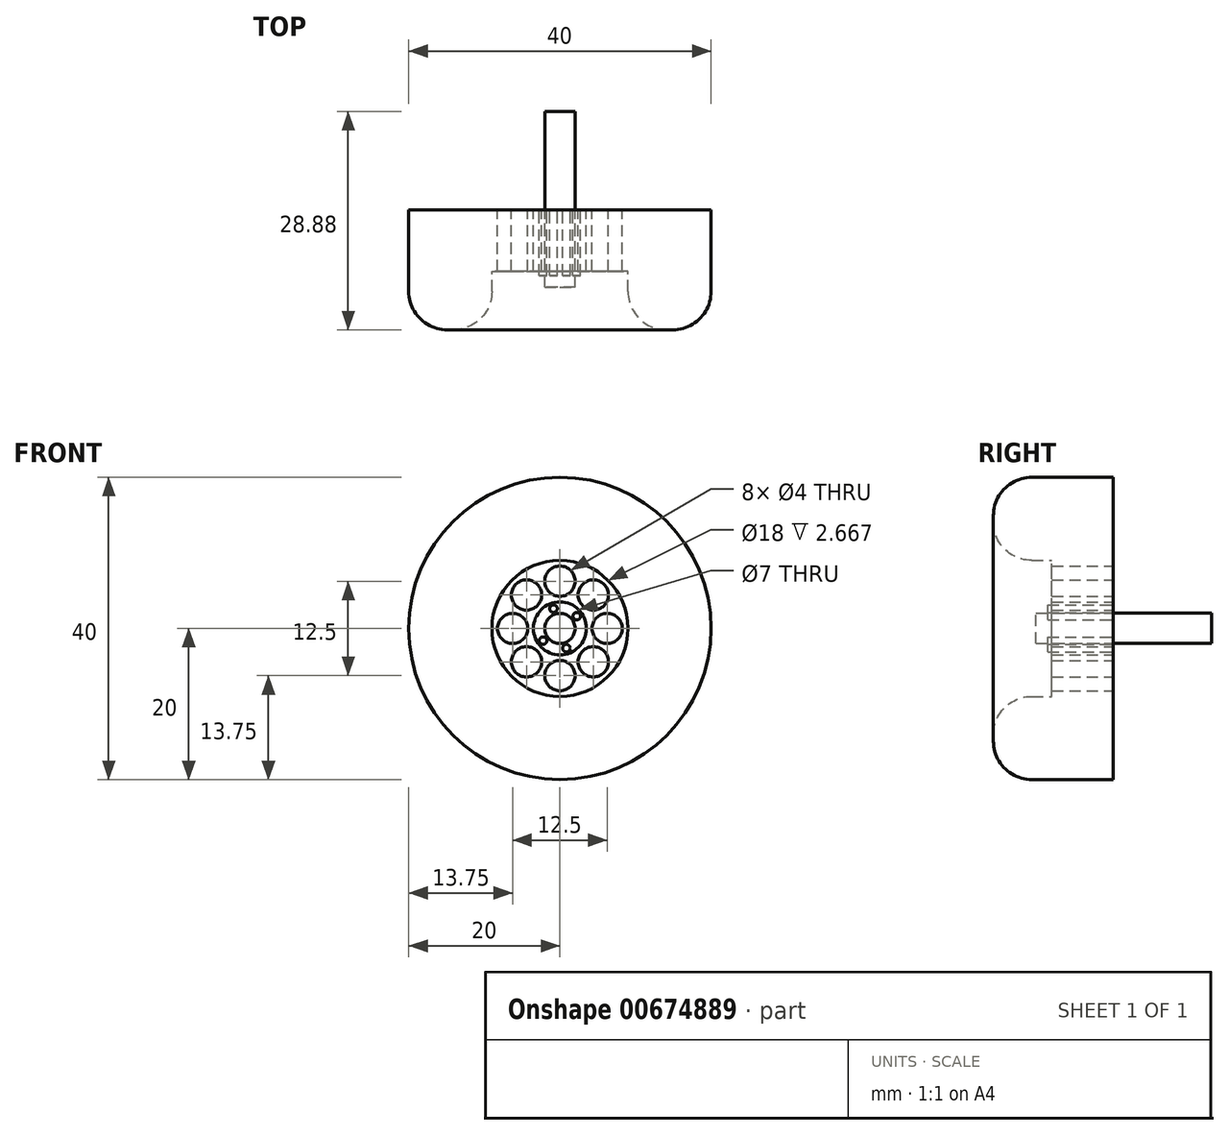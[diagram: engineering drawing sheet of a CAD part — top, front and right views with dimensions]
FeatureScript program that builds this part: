
annotation { "Feature Type Name" : "Feature", "Feature Type Description" : "" }
export const myFeature = defineFeature(function(context is Context, id is Id, definition is map)
    precondition{}
    {
        {
            var Q0;
            Q0=qCreatedBy(makeId("Front.planeOp"),FACE);
            var sketch = newSketch(context, id + "F0", { "sketchPlane" : qUnion([Q0])});
            skCircle(sketch, "E0", {"center": v(0, 0) * mm, "radius": 20 * mm});
            skSolve(sketch);
        }
        {
            var Q0;
            Q0=makeQuery(id+"F0.imprint","IMPRINT",FACE,{"disambiguationData":[TD([[makeQuery(id+"F0.imprint","IMPRINT",EDGE,{"derivedFrom":sQuery(id+"F0.wireOp",EDGE,"E0")}),1.0]])]});
            var sketch = newSketch(context, id + "F1", { "sketchPlane" : qUnion([Q0])});
            skCircle(sketch, "E1", {"center": v(0, 0) * mm, "radius": 3.5 * mm});
            skCircle(sketch, "E2", {"center": v(0, 0) * mm, "radius": 18 * mm});
            skCircle(sketch, "E3", {"center": v(0, 0) * mm, "radius": 2 * mm});
            skLineSegment(sketch, "E4", {"start": v(0, 18) * mm, "end": v(0, -18) * mm});
            skLineSegment(sketch, "E5", {"start": v(-18, 0) * mm, "end": v(18, 0) * mm});
            skCircle(sketch, "E6", {"center": v(0, 0) * mm, "radius": 9 * mm});
            skCircle(sketch, "E7", {"center": v(-2.75, 0) * mm, "radius": 0.5 * mm});
            skCircle(sketch, "E8", {"center": v(0, 6.25) * mm, "radius": 2 * mm});
            skCircle(sketch, "E9.1.0", {"center": v(-4.42, 4.42) * mm, "radius": 2 * mm});
            skCircle(sketch, "E9.2.0", {"center": v(-6.25, 0) * mm, "radius": 2 * mm});
            skCircle(sketch, "E9.3.0", {"center": v(-4.42, -4.42) * mm, "radius": 2 * mm});
            skCircle(sketch, "E9.4.0", {"center": v(0, -6.25) * mm, "radius": 2 * mm});
            skCircle(sketch, "E9.5.0", {"center": v(4.42, -4.42) * mm, "radius": 2 * mm});
            skCircle(sketch, "E9.6.0", {"center": v(6.25, 0) * mm, "radius": 2 * mm});
            skCircle(sketch, "E9.7.0", {"center": v(4.42, 4.42) * mm, "radius": 2 * mm});
            skCircle(sketch, "E10.1.0", {"center": v(-2.22, -1.62) * mm, "radius": 0.5 * mm});
            skCircle(sketch, "E10.2.0", {"center": v(-0.85, -2.62) * mm, "radius": 0.5 * mm});
            skCircle(sketch, "E10.3.0", {"center": v(0.85, -2.62) * mm, "radius": 0.5 * mm});
            skCircle(sketch, "E10.4.0", {"center": v(2.22, -1.62) * mm, "radius": 0.5 * mm});
            skCircle(sketch, "E10.5.0", {"center": v(2.75, 0) * mm, "radius": 0.5 * mm});
            skCircle(sketch, "E10.6.0", {"center": v(2.22, 1.62) * mm, "radius": 0.5 * mm});
            skCircle(sketch, "E10.7.0", {"center": v(0.85, 2.62) * mm, "radius": 0.5 * mm});
            skCircle(sketch, "E10.8.0", {"center": v(-0.85, 2.62) * mm, "radius": 0.5 * mm});
            skCircle(sketch, "E10.9.0", {"center": v(-2.22, 1.62) * mm, "radius": 0.5 * mm});
            skSolve(sketch);
        }
        {
            var Q0;
            Q0=makeQuery(id+"F1.imprint","IMPRINT",FACE,{"disambiguationData":[TD([[makeQuery(id+"F1.imprint","IMPRINT",EDGE,{"derivedFrom":makeQuery(id+"F0.imprint","IMPRINT",EDGE,{"derivedFrom":sQuery(id+"F0.wireOp",EDGE,"E0")})}),1.0]])]});
            extrude(context, id + "F2", {"entities" : qUnion([Q0]), "depth" : 15.88 * mm, "offsetDistance" : 25.4 * mm});
        }
        {
            var Q0;
            Q0 = qSketchRegion(id + "F1", true);
            extrude(context, id + "F3", {"entities" : qUnion([Q0]), "operationType" : NewBodyOperationType.ADD, "depth" : 15.88 * mm, "offsetDistance" : 25.4 * mm});
        }
        {
            var Q0;
            Q0=makeQuery(id+"F1.imprint","IMPRINT",FACE,{"disambiguationData":[TD([[makeQuery(id+"F1.imprint","IMPRINT",EDGE,{"derivedFrom":sQuery(id+"F1.wireOp",EDGE,"E9.1.0")}),-1.0]])]});
            var Q1;
            Q1=makeQuery(id+"F1.imprint","IMPRINT",FACE,{"disambiguationData":[TD([[makeQuery(id+"F1.imprint","IMPRINT",EDGE,{"derivedFrom":sQuery(id+"F1.wireOp",EDGE,"E9.7.0")}),-1.0]])]});
            var Q2;
            Q2=makeQuery(id+"F1.imprint","IMPRINT",FACE,{"disambiguationData":[TD([[makeQuery(id+"F1.imprint","IMPRINT",EDGE,{"derivedFrom":sQuery(id+"F1.wireOp",EDGE,"E9.5.0")}),-1.0]])]});
            var Q3;
            Q3=makeQuery(id+"F1.imprint","IMPRINT",FACE,{"disambiguationData":[TD([[makeQuery(id+"F1.imprint","IMPRINT",EDGE,{"derivedFrom":sQuery(id+"F1.wireOp",EDGE,"E9.3.0")}),-1.0]])]});
            extrude(context, id + "F4", {"entities" : qUnion([Q0, Q1, Q2, Q3]), "operationType" : NewBodyOperationType.ADD, "depth" : 8.13 * mm, "offsetDistance" : 25.4 * mm});
        }
        {
            var Q0;
            Q0=makeQuery(id+"F1.imprint","IMPRINT",FACE,{"disambiguationData":[TD([[makeQuery(id+"F1.imprint","IMPRINT",EDGE,{"derivedFrom":sQuery(id+"F1.wireOp",EDGE,"E9.3.0")}),-1.0]])]});
            var Q1;
            Q1=makeQuery(id+"F1.imprint","IMPRINT",FACE,{"disambiguationData":[TD([[makeQuery(id+"F1.imprint","IMPRINT",EDGE,{"derivedFrom":sQuery(id+"F1.wireOp",EDGE,"E9.5.0")}),-1.0]])]});
            var Q2;
            Q2=makeQuery(id+"F1.imprint","IMPRINT",FACE,{"disambiguationData":[TD([[makeQuery(id+"F1.imprint","IMPRINT",EDGE,{"derivedFrom":sQuery(id+"F1.wireOp",EDGE,"E9.7.0")}),-1.0]])]});
            var Q3;
            Q3=makeQuery(id+"F1.imprint","IMPRINT",FACE,{"disambiguationData":[TD([[makeQuery(id+"F1.imprint","IMPRINT",EDGE,{"derivedFrom":sQuery(id+"F1.wireOp",EDGE,"E9.1.0")}),-1.0]])]});
            extrude(context, id + "F5", {"entities" : qUnion([Q0, Q1, Q2, Q3]), "operationType" : NewBodyOperationType.REMOVE, "oppositeDirection" : true, "depth" : 10 * mm, "offsetDistance" : 25.4 * mm});
        }
        {
            var Q0;
            {var subQ0=sQuery(id+"F1.wireOp",EDGE,"E5");var subQ1=sQuery(id+"F1.wireOp",EDGE,"E3");var subQ2=makeQuery(id+"F1.imprint","INTERSECT",VERTEX,{"disambiguationData":[OD(0.0)],"derivedFrom":[subQ1,subQ0]});Q0=makeQuery(id+"F1.imprint","IMPRINT",FACE,{"disambiguationData":[TD([[makeQuery(id+"F1.imprint","IMPRINT",EDGE,{"disambiguationData":[TD([[subQ2,1.0]])],"derivedFrom":subQ1}),1.0]])]});}
            var Q1;
            {var subQ0=sQuery(id+"F1.wireOp",EDGE,"E5");var subQ1=sQuery(id+"F1.wireOp",EDGE,"E3");var subQ2=makeQuery(id+"F1.imprint","INTERSECT",VERTEX,{"disambiguationData":[OD(1.0)],"derivedFrom":[subQ1,subQ0]});Q1=makeQuery(id+"F1.imprint","IMPRINT",FACE,{"disambiguationData":[TD([[makeQuery(id+"F1.imprint","IMPRINT",EDGE,{"disambiguationData":[TD([[subQ2,-1.0]])],"derivedFrom":subQ1}),1.0]])]});}
            var Q2;
            {var subQ0=sQuery(id+"F1.wireOp",EDGE,"E4");var subQ1=sQuery(id+"F1.wireOp",EDGE,"E3");var subQ2=makeQuery(id+"F1.imprint","INTERSECT",VERTEX,{"disambiguationData":[OD(0.0)],"derivedFrom":[subQ1,subQ0]});Q2=makeQuery(id+"F1.imprint","IMPRINT",FACE,{"disambiguationData":[TD([[makeQuery(id+"F1.imprint","IMPRINT",EDGE,{"disambiguationData":[TD([[subQ2,-1.0]])],"derivedFrom":subQ1}),1.0]])]});}
            var Q3;
            {var subQ0=sQuery(id+"F1.wireOp",EDGE,"E4");var subQ1=sQuery(id+"F1.wireOp",EDGE,"E3");var subQ2=makeQuery(id+"F1.imprint","INTERSECT",VERTEX,{"disambiguationData":[OD(0.0)],"derivedFrom":[subQ1,subQ0]});Q3=makeQuery(id+"F1.imprint","IMPRINT",FACE,{"disambiguationData":[TD([[makeQuery(id+"F1.imprint","IMPRINT",EDGE,{"disambiguationData":[TD([[subQ2,1.0]])],"derivedFrom":subQ1}),1.0]])]});}
            extrude(context, id + "F6", {"entities" : qUnion([Q0, Q1, Q2, Q3]), "oppositeDirection" : true, "depth" : 13 * mm, "offsetDistance" : 25.4 * mm});
        }
        {
            var Q0;
            Q0=makeQuery(id+"F1.imprint","IMPRINT",FACE,{"disambiguationData":[TD([[makeQuery(id+"F1.imprint","IMPRINT",EDGE,{"derivedFrom":sQuery(id+"F1.wireOp",EDGE,"E10.6.0")}),1.0]])]});
            var Q1;
            Q1=makeQuery(id+"F1.imprint","IMPRINT",FACE,{"disambiguationData":[TD([[makeQuery(id+"F1.imprint","IMPRINT",EDGE,{"derivedFrom":sQuery(id+"F1.wireOp",EDGE,"E10.8.0")}),1.0]])]});
            var Q2;
            Q2=makeQuery(id+"F1.imprint","IMPRINT",FACE,{"disambiguationData":[TD([[makeQuery(id+"F1.imprint","IMPRINT",EDGE,{"derivedFrom":sQuery(id+"F1.wireOp",EDGE,"E10.1.0")}),1.0]])]});
            var Q3;
            Q3=makeQuery(id+"F1.imprint","IMPRINT",FACE,{"disambiguationData":[TD([[makeQuery(id+"F1.imprint","IMPRINT",EDGE,{"derivedFrom":sQuery(id+"F1.wireOp",EDGE,"E10.3.0")}),1.0]])]});
            extrude(context, id + "F7", {"entities" : qUnion([Q0, Q1, Q2, Q3]), "depth" : 8.7 * mm, "offsetDistance" : 25.4 * mm});
        }
        {
            var Q0;
            {var subQ0=sQuery(id+"F1.wireOp",EDGE,"E5");var subQ1=sQuery(id+"F1.wireOp",EDGE,"E3");var subQ2=makeQuery(id+"F1.imprint","INTERSECT",VERTEX,{"disambiguationData":[OD(1.0)],"derivedFrom":[subQ1,subQ0]});Q0=makeQuery(id+"F1.imprint","IMPRINT",FACE,{"disambiguationData":[TD([[makeQuery(id+"F1.imprint","IMPRINT",EDGE,{"disambiguationData":[TD([[subQ2,-1.0]])],"derivedFrom":subQ1}),1.0]])]});}
            var Q1;
            {var subQ0=sQuery(id+"F1.wireOp",EDGE,"E4");var subQ1=sQuery(id+"F1.wireOp",EDGE,"E3");var subQ2=makeQuery(id+"F1.imprint","INTERSECT",VERTEX,{"disambiguationData":[OD(0.0)],"derivedFrom":[subQ1,subQ0]});Q1=makeQuery(id+"F1.imprint","IMPRINT",FACE,{"disambiguationData":[TD([[makeQuery(id+"F1.imprint","IMPRINT",EDGE,{"disambiguationData":[TD([[subQ2,-1.0]])],"derivedFrom":subQ1}),1.0]])]});}
            var Q2;
            {var subQ0=sQuery(id+"F1.wireOp",EDGE,"E4");var subQ1=sQuery(id+"F1.wireOp",EDGE,"E3");var subQ2=makeQuery(id+"F1.imprint","INTERSECT",VERTEX,{"disambiguationData":[OD(0.0)],"derivedFrom":[subQ1,subQ0]});Q2=makeQuery(id+"F1.imprint","IMPRINT",FACE,{"disambiguationData":[TD([[makeQuery(id+"F1.imprint","IMPRINT",EDGE,{"disambiguationData":[TD([[subQ2,1.0]])],"derivedFrom":subQ1}),1.0]])]});}
            var Q3;
            {var subQ0=sQuery(id+"F1.wireOp",EDGE,"E5");var subQ1=sQuery(id+"F1.wireOp",EDGE,"E3");var subQ2=makeQuery(id+"F1.imprint","INTERSECT",VERTEX,{"disambiguationData":[OD(0.0)],"derivedFrom":[subQ1,subQ0]});Q3=makeQuery(id+"F1.imprint","IMPRINT",FACE,{"disambiguationData":[TD([[makeQuery(id+"F1.imprint","IMPRINT",EDGE,{"disambiguationData":[TD([[subQ2,1.0]])],"derivedFrom":subQ1}),1.0]])]});}
            extrude(context, id + "F8", {"entities" : qUnion([Q0, Q1, Q2, Q3]), "depth" : 10.21 * mm, "offsetDistance" : 25.4 * mm});
        }
        {
            var Q0;
            {var subQ0=sQuery(id+"F1.wireOp",EDGE,"E2");Q0=makeQuery(id+"F3.boolean.opBoolean","MERGE",FACE,{"derivedFrom":[makeQuery(id+"F2.opExtrude","CAP_FACE",FACE,{"disambiguationData":[OSD([sQuery(id+"F0.wireOp",EDGE,"E0"),subQ0])],"isStart":false}),makeQuery(id+"F3.opExtrude","CAP_FACE",FACE,{"disambiguationData":[OSD([subQ0,sQuery(id+"F1.wireOp",EDGE,"E6")])],"isStart":false})]});}
            fillet(context, id + "F9", {"entities" : qUnion([Q0]), "radius" : 5.08 * mm, "tangentPropagation" : true, "allowEdgeOverflow" : false});
        }
    });
